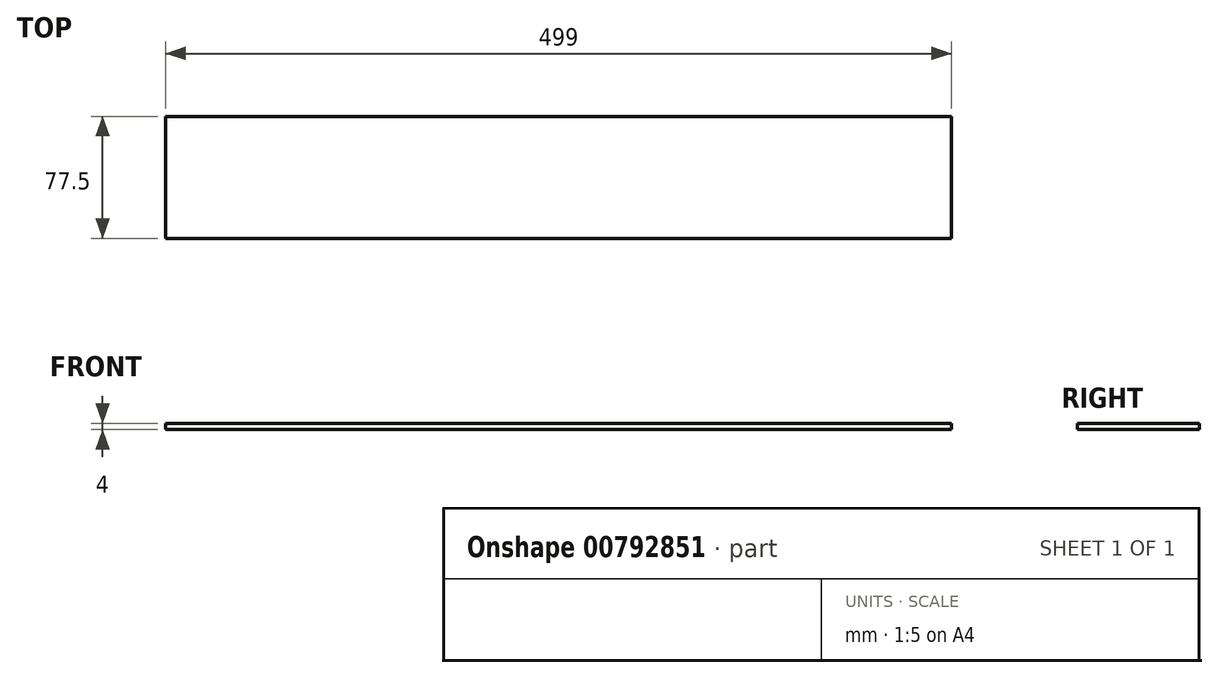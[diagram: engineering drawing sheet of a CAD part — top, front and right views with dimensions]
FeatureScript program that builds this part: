
annotation { "Feature Type Name" : "Feature", "Feature Type Description" : "" }
export const myFeature = defineFeature(function(context is Context, id is Id, definition is map)
    precondition{}
    {
        {
            var Q0;
            Q0=qCreatedBy(makeId("Top.planeOp"),FACE);
            var sketch = newSketch(context, id + "F0", { "sketchPlane" : qUnion([Q0])});
            skLineSegment(sketch, "E0.bottom", {"start": v(249.5, -38.75) * mm, "end": v(-249.5, -38.75) * mm});
            skLineSegment(sketch, "E0.top", {"start": v(249.5, 38.75) * mm, "end": v(-249.5, 38.75) * mm});
            skLineSegment(sketch, "E0.left", {"start": v(249.5, -38.75) * mm, "end": v(249.5, 38.75) * mm});
            skLineSegment(sketch, "E0.right", {"start": v(-249.5, -38.75) * mm, "end": v(-249.5, 38.75) * mm});
            skPoint(sketch, "E0.middle", {"position": v(0, 0) * mm});
            skSolve(sketch);
        }
        {
            var Q0;
            Q0 = qSketchRegion(id + "F0", true);
            extrude(context, id + "F1", {"entities" : qUnion([Q0]), "depth" : 4 * mm, "offsetDistance" : 25 * mm});
        }
    });
